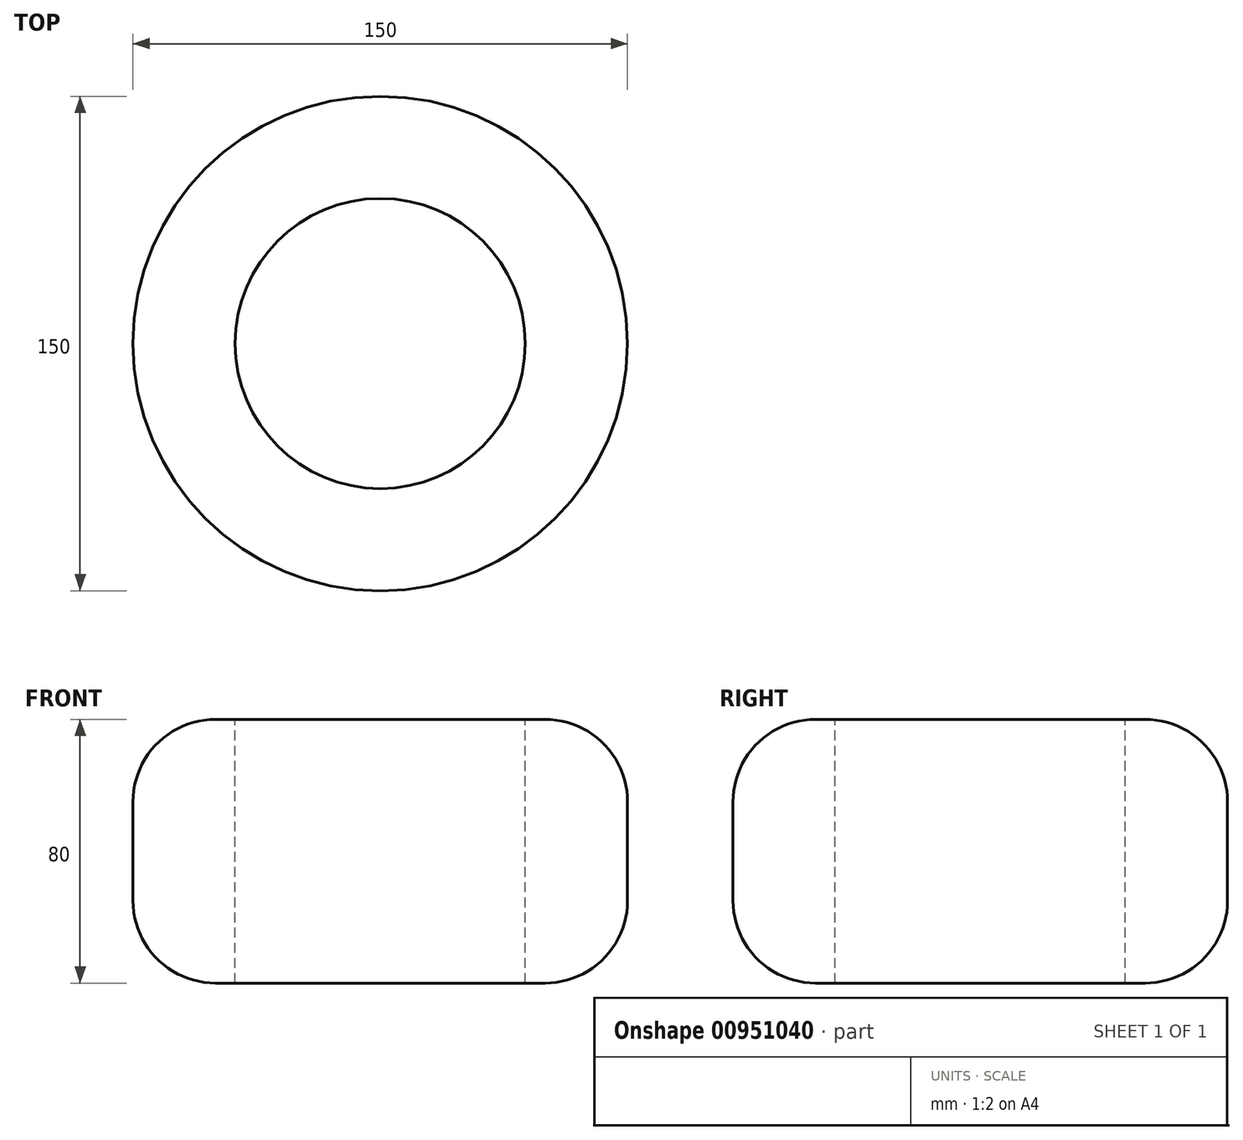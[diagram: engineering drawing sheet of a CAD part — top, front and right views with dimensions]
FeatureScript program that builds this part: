
annotation { "Feature Type Name" : "Feature", "Feature Type Description" : "" }
export const myFeature = defineFeature(function(context is Context, id is Id, definition is map)
    precondition{}
    {
        {
            var Q0;
            Q0=qCreatedBy(makeId("Top.planeOp"),FACE);
            var sketch = newSketch(context, id + "F0", { "sketchPlane" : qUnion([Q0])});
            skCircle(sketch, "E0", {"center": v(0, 0) * mm, "radius": 75 * mm});
            skSolve(sketch);
        }
        {
            var Q0;
            Q0=makeQuery(id+"F0.imprint","IMPRINT",FACE,{"disambiguationData":[TD([[makeQuery(id+"F0.imprint","IMPRINT",EDGE,{"derivedFrom":sQuery(id+"F0.wireOp",EDGE,"E0")}),1.0]])]});
            extrude(context, id + "F1", {"entities" : qUnion([Q0]), "depth" : 80 * mm, "offsetDistance" : 25 * mm});
        }
        {
            var Q0;
            Q0=makeQuery(id+"F1.opExtrude","SWEPT_FACE",FACE,{"disambiguationData":[OSD([sQuery(id+"F0.wireOp",EDGE,"E0")])]});
            fillet(context, id + "F2", {"entities" : qUnion([Q0]), "tangentPropagation" : true, "radius" : 25 * mm, "defaultsChanged" : true, "vertexSettings" : [], "allowEdgeOverflow" : false});
        }
        {
            var Q0;
            Q0=makeQuery(id+"F1.opExtrude","CAP_FACE",FACE,{"disambiguationData":[OSD([sQuery(id+"F0.wireOp",EDGE,"E0")])],"isStart":false});
            var sketch = newSketch(context, id + "F3", { "sketchPlane" : qUnion([Q0])});
            skCircle(sketch, "E1", {"center": v(0, 0) * mm, "radius": 44 * mm});
            skSolve(sketch);
        }
        {
            var Q0;
            Q0 = qSketchRegion(id + "F3", true);
            extrude(context, id + "F4", {"entities" : qUnion([Q0]), "operationType" : NewBodyOperationType.REMOVE, "oppositeDirection" : true, "depth" : 177.9 * mm, "offsetDistance" : 25 * mm});
        }
    });
